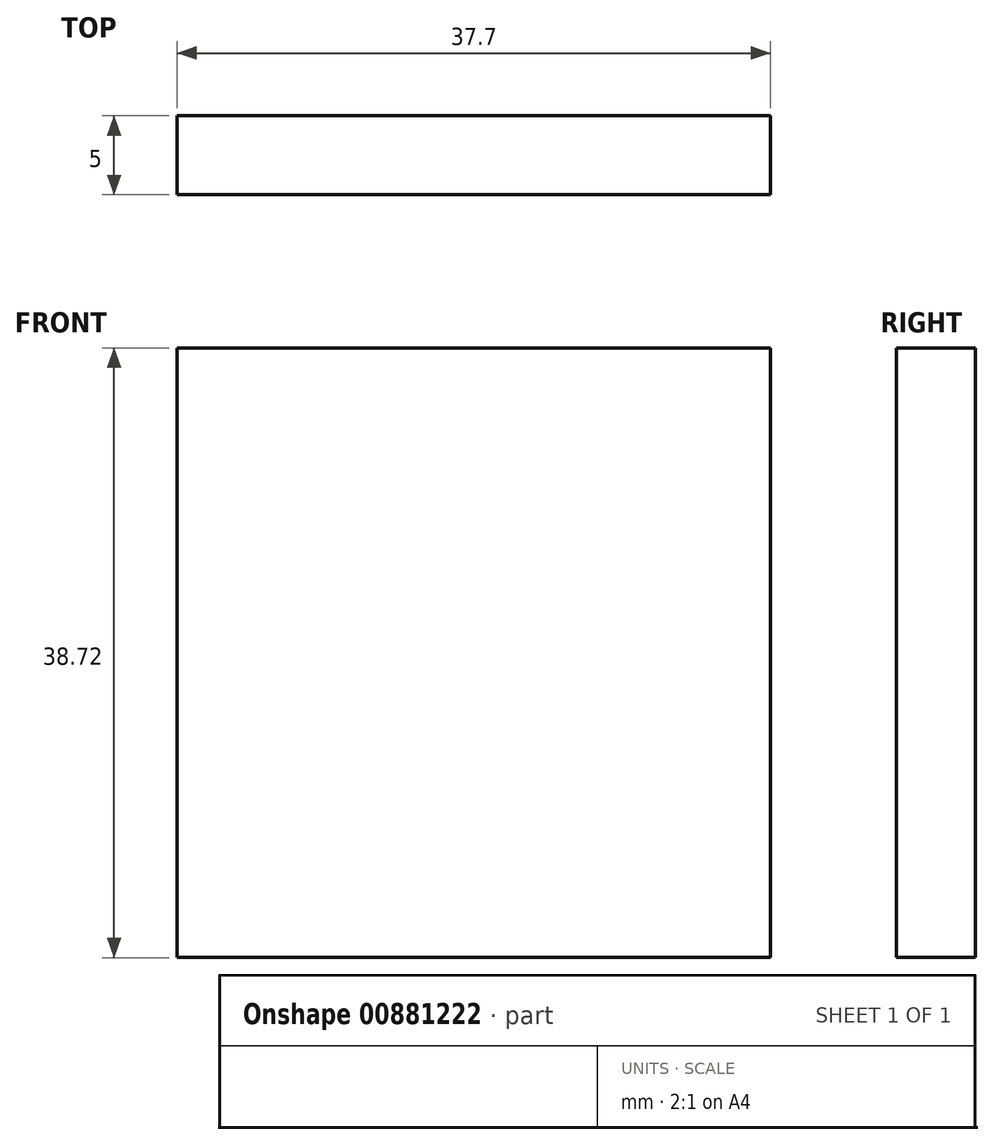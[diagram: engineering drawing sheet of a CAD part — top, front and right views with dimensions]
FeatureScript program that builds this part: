
annotation { "Feature Type Name" : "Feature", "Feature Type Description" : "" }
export const myFeature = defineFeature(function(context is Context, id is Id, definition is map)
    precondition{}
    {
        {
            var Q0;
            Q0=qCreatedBy(makeId("Front.planeOp"),FACE);
            var sketch = newSketch(context, id + "F0", { "sketchPlane" : qUnion([Q0])});
            skCircle(sketch, "E0", {"center": v(2.88, 0) * mm, "radius": 53.63 * mm});
            skSolve(sketch);
        }
        {
            var Q0;
            Q0 = qSketchRegion(id + "F0", true);
            extrude(context, id + "F1", {"entities" : qUnion([Q0]), "endBound" : BoundingType.SYMMETRIC, "depth" : 5 * mm, "offsetDistance" : 25.4 * mm});
        }
        {
            var Q0;
            Q0=makeQuery(id+"F1.opExtrude","CAP_FACE",FACE,{"disambiguationData":[OSD([sQuery(id+"F0.wireOp",EDGE,"E0")])],"isStart":false});
            var sketch = newSketch(context, id + "F2", { "sketchPlane" : qUnion([Q0])});
            skLineSegment(sketch, "E1.bottom", {"start": v(18.85, -19.36) * mm, "end": v(-18.85, -19.36) * mm});
            skLineSegment(sketch, "E1.top", {"start": v(18.85, 19.36) * mm, "end": v(-18.85, 19.36) * mm});
            skLineSegment(sketch, "E1.left", {"start": v(18.85, -19.36) * mm, "end": v(18.85, 19.36) * mm});
            skLineSegment(sketch, "E1.right", {"start": v(-18.85, -19.36) * mm, "end": v(-18.85, 19.36) * mm});
            skPoint(sketch, "E1.middle", {"position": v(0, 0) * mm});
            skSolve(sketch);
        }
        {
            var Q0;
            Q0=makeQuery(id+"F2.imprint","IMPRINT",FACE,{"disambiguationData":[TD([[makeQuery(id+"F2.imprint","IMPRINT",EDGE,{"derivedFrom":sQuery(id+"F2.wireOp",EDGE,"E1.bottom")}),-1.0]])]});
            extrude(context, id + "F3", {"entities" : qUnion([Q0]), "operationType" : NewBodyOperationType.INTERSECT, "depth" : 40 * mm, "offsetDistance" : 25.4 * mm, "hasSecondDirection" : true, "secondDirectionOppositeDirection" : true, "secondDirectionDepth" : 40 * mm});
        }
    });
